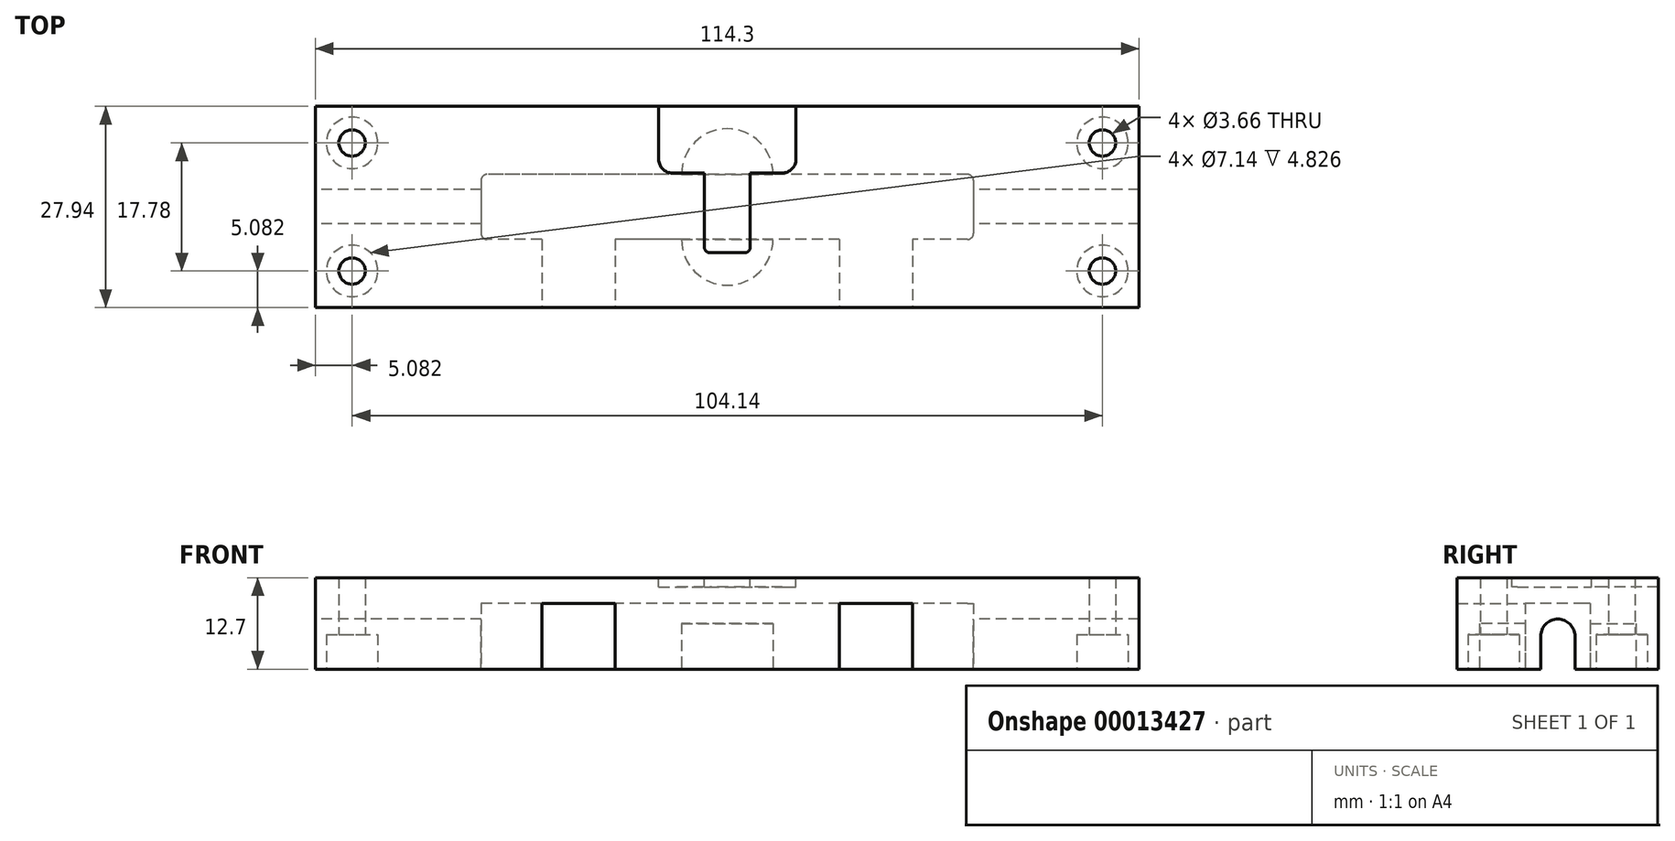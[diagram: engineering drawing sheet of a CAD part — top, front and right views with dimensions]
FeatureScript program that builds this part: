
annotation { "Feature Type Name" : "Feature", "Feature Type Description" : "" }
export const myFeature = defineFeature(function(context is Context, id is Id, definition is map)
    precondition{}
    {
        {
            var Q0;
            Q0=qCreatedBy(makeId("Top.planeOp"),FACE);
            var sketch = newSketch(context, id + "F0", { "sketchPlane" : qUnion([Q0])});
            skLineSegment(sketch, "E0.bottom", {"start": v(-44.98, -11.5) * mm, "end": v(69.32, -11.5) * mm});
            skLineSegment(sketch, "E0.top", {"start": v(-44.98, 16.43) * mm, "end": v(69.32, 16.43) * mm});
            skLineSegment(sketch, "E0.left", {"start": v(-44.98, -11.5) * mm, "end": v(-44.98, 16.43) * mm});
            skLineSegment(sketch, "E0.right", {"start": v(69.32, -11.5) * mm, "end": v(69.32, 16.43) * mm});
            skSolve(sketch);
        }
        {
            var Q0;
            Q0=makeQuery(id+"F0.imprint","IMPRINT",FACE,{"disambiguationData":[TD([[makeQuery(id+"F0.imprint","IMPRINT",EDGE,{"derivedFrom":sQuery(id+"F0.wireOp",EDGE,"E0.bottom")}),1.0]])]});
            extrude(context, id + "F1", {"entities" : qUnion([Q0]), "depth" : 12.7 * mm});
        }
        {
            var Q0;
            Q0=makeQuery(id+"F1.opExtrude","CAP_FACE",FACE,{"disambiguationData":[OSD([sQuery(id+"F0.wireOp",EDGE,"E0.bottom"),sQuery(id+"F0.wireOp",EDGE,"E0.top"),sQuery(id+"F0.wireOp",EDGE,"E0.left"),sQuery(id+"F0.wireOp",EDGE,"E0.right")])],"isStart":true});
            var sketch = newSketch(context, id + "F2", { "sketchPlane" : qUnion([Q0])});
            skLineSegment(sketch, "E1.bottom", {"start": v(45.52, -6.97) * mm, "end": v(-21.18, -6.97) * mm});
            skLineSegment(sketch, "E1.top", {"start": v(45.52, 2.05) * mm, "end": v(-21.18, 2.05) * mm});
            skLineSegment(sketch, "E1.left", {"start": v(46.33, -6.16) * mm, "end": v(46.33, 1.23) * mm});
            skLineSegment(sketch, "E1.right", {"start": v(-22, -6.16) * mm, "end": v(-22, 1.23) * mm});
            skPoint(sketch, "E2.visualSharp", {"position": v(46.33, -6.97) * mm});
            skArc(sketch, "E2.filletArc", {"start": v(45.52, -6.97) * mm, "mid": v(46.1, -6.73) * mm, "end": v(46.33, -6.16) * mm});
            skPoint(sketch, "E3.visualSharp", {"position": v(46.33, 2.05) * mm});
            skArc(sketch, "E3.filletArc", {"start": v(46.33, 1.23) * mm, "mid": v(46.1, 1.8) * mm, "end": v(45.52, 2.05) * mm});
            skPoint(sketch, "E4.visualSharp", {"position": v(-22, -6.97) * mm});
            skArc(sketch, "E4.filletArc", {"start": v(-22, -6.16) * mm, "mid": v(-21.75, -6.73) * mm, "end": v(-21.18, -6.97) * mm});
            skPoint(sketch, "E5.visualSharp", {"position": v(-22, 2.05) * mm});
            skArc(sketch, "E5.filletArc", {"start": v(-21.18, 2.05) * mm, "mid": v(-21.75, 1.8) * mm, "end": v(-22, 1.23) * mm});
            skSolve(sketch);
        }
        {
            var Q0;
            Q0=qSketchRegion(id+"F2",true);
            extrude(context, id + "F3", {"entities" : qUnion([Q0]), "operationType" : NewBodyOperationType.REMOVE, "oppositeDirection" : true, "depth" : 9.14 * mm});
        }
        {
            var Q0;
            Q0=makeQuery(id+"F1.opExtrude","SWEPT_FACE",FACE,{"disambiguationData":[OSD([sQuery(id+"F0.wireOp",EDGE,"E0.left")])]});
            var sketch = newSketch(context, id + "F4", { "sketchPlane" : qUnion([Q0])});
            skArc(sketch, "E6", {"start": v(-0.1, 4.57) * mm, "mid": v(-2.49, 6.95) * mm, "end": v(-4.87, 4.57) * mm});
            skLineSegment(sketch, "E7", {"start": v(-4.87, 4.57) * mm, "end": v(-4.87, 0) * mm});
            skLineSegment(sketch, "E8", {"start": v(-4.87, 0) * mm, "end": v(-0.1, 0) * mm});
            skLineSegment(sketch, "E9", {"start": v(-0.1, 0) * mm, "end": v(-0.1, 4.57) * mm});
            skSolve(sketch);
        }
        {
            var Q0;
            Q0=qSketchRegion(id+"F4",true);
            extrude(context, id + "F5", {"entities" : qUnion([Q0]), "operationType" : NewBodyOperationType.REMOVE, "endBound" : BoundingType.THROUGH_ALL, "oppositeDirection" : true, "depth" : 25.4 * mm});
        }
        {
            var Q0;
            {var subQ0=sQuery(id+"F0.wireOp",EDGE,"E0.bottom");var subQ1=sQuery(id+"F0.wireOp",EDGE,"E0.left");var subQ2=sQuery(id+"F0.wireOp",EDGE,"E0.right");Q0=makeQuery(id+"F5.boolean.opBoolean","SPLIT",FACE,{"disambiguationData":[TD([makeQuery(id+"F1.opExtrude","SWEPT_FACE",FACE,{"disambiguationData":[OSD([subQ0])]})])],"derivedFrom":makeQuery(id+"F1.opExtrude","CAP_FACE",FACE,{"disambiguationData":[OSD([subQ0,sQuery(id+"F0.wireOp",EDGE,"E0.top"),subQ1,subQ2])],"isStart":true})});}
            var sketch = newSketch(context, id + "F6", { "sketchPlane" : qUnion([Q0])});
            skArc(sketch, "E10", {"start": v(18.52, 2.05) * mm, "mid": v(12.17, 8.4) * mm, "end": v(5.82, 2.05) * mm});
            skArc(sketch, "E11", {"start": v(5.82, -6.97) * mm, "mid": v(12.17, -13.32) * mm, "end": v(18.52, -6.97) * mm});
            skLineSegment(sketch, "E12", {"start": v(5.82, 2.05) * mm, "end": v(5.82, -6.97) * mm});
            skLineSegment(sketch, "E13", {"start": v(18.52, 2.05) * mm, "end": v(18.52, -6.97) * mm});
            skSolve(sketch);
        }
        {
            var Q0;
            Q0=qSketchRegion(id+"F6",true);
            extrude(context, id + "F7", {"entities" : qUnion([Q0]), "operationType" : NewBodyOperationType.REMOVE, "oppositeDirection" : true, "depth" : 6.35 * mm});
        }
        {
            var Q0;
            {var subQ0=sQuery(id+"F0.wireOp",EDGE,"E0.bottom");var subQ1=sQuery(id+"F0.wireOp",EDGE,"E0.left");var subQ2=sQuery(id+"F0.wireOp",EDGE,"E0.right");Q0=makeQuery(id+"F5.boolean.opBoolean","SPLIT",FACE,{"disambiguationData":[TD([makeQuery(id+"F1.opExtrude","SWEPT_FACE",FACE,{"disambiguationData":[OSD([subQ0])]})])],"derivedFrom":makeQuery(id+"F1.opExtrude","CAP_FACE",FACE,{"disambiguationData":[OSD([subQ0,sQuery(id+"F0.wireOp",EDGE,"E0.top"),subQ1,subQ2])],"isStart":true})});}
            var sketch = newSketch(context, id + "F8", { "sketchPlane" : qUnion([Q0])});
            skLineSegment(sketch, "E14.top", {"start": v(37.9, 11.5) * mm, "end": v(27.74, 11.5) * mm});
            skLineSegment(sketch, "E14.left", {"start": v(37.9, 2.05) * mm, "end": v(37.9, 11.5) * mm});
            skLineSegment(sketch, "E14.right", {"start": v(27.74, 2.05) * mm, "end": v(27.74, 11.5) * mm});
            skLineSegment(sketch, "E15", {"start": v(37.9, 2.05) * mm, "end": v(27.74, 2.05) * mm});
            skSolve(sketch);
        }
        {
            var Q0;
            Q0=qSketchRegion(id+"F8",true);
            var Q1;
            Q1=makeQuery(id+"F3.boolean.opBoolean","COPY",FACE,{"derivedFrom":makeQuery(id+"F3.opExtrude","CAP_FACE",FACE,{"disambiguationData":[OSD([sQuery(id+"F2.wireOp",EDGE,"E1.bottom"),sQuery(id+"F2.wireOp",EDGE,"E1.top"),sQuery(id+"F2.wireOp",EDGE,"E1.left"),sQuery(id+"F2.wireOp",EDGE,"E1.right"),sQuery(id+"F2.wireOp",EDGE,"E2.filletArc"),sQuery(id+"F2.wireOp",EDGE,"E3.filletArc"),sQuery(id+"F2.wireOp",EDGE,"E4.filletArc"),sQuery(id+"F2.wireOp",EDGE,"E5.filletArc")])],"isStart":false})});
            extrude(context, id + "F9", {"entities" : qUnion([Q0]), "operationType" : NewBodyOperationType.REMOVE, "endBound" : BoundingType.UP_TO_SURFACE, "oppositeDirection" : true, "endBoundEntityFace" : qUnion([Q1]), "depth" : 25.4 * mm});
        }
        {
            var Q0;
            {var subQ0=sQuery(id+"F0.wireOp",EDGE,"E0.bottom");var subQ1=sQuery(id+"F0.wireOp",EDGE,"E0.left");var subQ2=sQuery(id+"F0.wireOp",EDGE,"E0.right");var subQ7=makeQuery(id+"F1.opExtrude","SWEPT_FACE",FACE,{"disambiguationData":[OSD([subQ1])]});var subQ8=makeQuery(id+"F1.opExtrude","SWEPT_FACE",FACE,{"disambiguationData":[OSD([subQ0])]});Q0=makeQuery(id+"F9.boolean.opBoolean","SPLIT",FACE,{"disambiguationData":[TD([subQ7])],"derivedFrom":makeQuery(id+"F5.boolean.opBoolean","SPLIT",FACE,{"disambiguationData":[TD([subQ8])],"derivedFrom":makeQuery(id+"F1.opExtrude","CAP_FACE",FACE,{"disambiguationData":[OSD([subQ0,sQuery(id+"F0.wireOp",EDGE,"E0.top"),subQ1,subQ2])],"isStart":true})})});}
            var sketch = newSketch(context, id + "F10", { "sketchPlane" : qUnion([Q0])});
            skLineSegment(sketch, "E16.bottom", {"start": v(-3.4, 2.05) * mm, "end": v(-13.56, 2.05) * mm});
            skLineSegment(sketch, "E16.top", {"start": v(-3.4, 11.5) * mm, "end": v(-13.56, 11.5) * mm});
            skLineSegment(sketch, "E16.left", {"start": v(-3.4, 2.05) * mm, "end": v(-3.4, 11.5) * mm});
            skLineSegment(sketch, "E16.right", {"start": v(-13.56, 2.05) * mm, "end": v(-13.56, 11.5) * mm});
            skSolve(sketch);
        }
        {
            var Q0;
            Q0=qSketchRegion(id+"F10",true);
            var Q1;
            Q1=makeQuery(id+"F9.boolean.opBoolean","MERGE",FACE,{"derivedFrom":[makeQuery(id+"F3.boolean.opBoolean","COPY",FACE,{"derivedFrom":makeQuery(id+"F3.opExtrude","CAP_FACE",FACE,{"disambiguationData":[OSD([sQuery(id+"F2.wireOp",EDGE,"E1.bottom"),sQuery(id+"F2.wireOp",EDGE,"E1.top"),sQuery(id+"F2.wireOp",EDGE,"E1.left"),sQuery(id+"F2.wireOp",EDGE,"E1.right"),sQuery(id+"F2.wireOp",EDGE,"E2.filletArc"),sQuery(id+"F2.wireOp",EDGE,"E3.filletArc"),sQuery(id+"F2.wireOp",EDGE,"E4.filletArc"),sQuery(id+"F2.wireOp",EDGE,"E5.filletArc")])],"isStart":false})}),makeQuery(id+"F9.opExtrude","CAP_FACE",FACE,{"disambiguationData":[OSD([sQuery(id+"F8.wireOp",EDGE,"E14.top"),sQuery(id+"F8.wireOp",EDGE,"E14.left"),sQuery(id+"F8.wireOp",EDGE,"E14.right"),sQuery(id+"F8.wireOp",EDGE,"E15")])],"isStart":false})]});
            extrude(context, id + "F11", {"entities" : qUnion([Q0]), "operationType" : NewBodyOperationType.REMOVE, "endBound" : BoundingType.UP_TO_SURFACE, "oppositeDirection" : true, "endBoundEntityFace" : qUnion([Q1]), "depth" : 6.6 * mm});
        }
        {
            var Q0;
            {var subQ0=sQuery(id+"F0.wireOp",EDGE,"E0.top");var subQ1=sQuery(id+"F0.wireOp",EDGE,"E0.left");var subQ2=sQuery(id+"F0.wireOp",EDGE,"E0.right");Q0=makeQuery(id+"F5.boolean.opBoolean","SPLIT",FACE,{"disambiguationData":[TD([makeQuery(id+"F1.opExtrude","SWEPT_FACE",FACE,{"disambiguationData":[OSD([subQ0])]})])],"derivedFrom":makeQuery(id+"F1.opExtrude","CAP_FACE",FACE,{"disambiguationData":[OSD([sQuery(id+"F0.wireOp",EDGE,"E0.bottom"),subQ0,subQ1,subQ2])],"isStart":true})});}
            var sketch = newSketch(context, id + "F12", { "sketchPlane" : qUnion([Q0])});
            skPoint(sketch, "E17", {"position": v(64.24, -11.35) * mm});
            skPoint(sketch, "E18", {"position": v(64.24, 6.43) * mm});
            skPoint(sketch, "E19", {"position": v(-39.9, -11.35) * mm});
            skPoint(sketch, "E20", {"position": v(-39.9, 6.43) * mm});
            skSolve(sketch);
        }
        {
            var Q0;
            Q0=sQuery(id+"F12.wireOp",VERTEX,"E17");
            var Q1;
            Q1=sQuery(id+"F12.wireOp",VERTEX,"E18");
            var Q2;
            Q2=sQuery(id+"F12.wireOp",VERTEX,"E19");
            var Q3;
            Q3=sQuery(id+"F12.wireOp",VERTEX,"E20");
            var Q4;
            Q4=makeQuery(id+"FvrC87ADXBSDjqa_1.boolean.opBoolean","SPLIT",BODY,{"disambiguationData":[OD(0.0)],"derivedFrom":makeQuery(id+"F1.opExtrude","SWEPT_BODY",BODY,{"disambiguationData":[OSD([sQuery(id+"F0.wireOp",EDGE,"E0.bottom"),sQuery(id+"F0.wireOp",EDGE,"E0.top"),sQuery(id+"F0.wireOp",EDGE,"E0.left"),sQuery(id+"F0.wireOp",EDGE,"E0.right")])]})});
            hole(context, id + "F13", {"style" : HoleStyle.C_BORE, "holeDiameter" : 3.66 * mm, "cBoreDiameter" : 7.14 * mm, "cBoreDepth" : 4.83 * mm, "endStyle" : HoleEndStyle.THROUGH, "locations" : qUnion([Q0, Q1, Q2, Q3]), "scope" : qUnion([Q4])});
        }
        {
            var Q0;
            Q0=makeQuery(id+"F1.opExtrude","CAP_FACE",FACE,{"disambiguationData":[OSD([sQuery(id+"F0.wireOp",EDGE,"E0.bottom"),sQuery(id+"F0.wireOp",EDGE,"E0.top"),sQuery(id+"F0.wireOp",EDGE,"E0.left"),sQuery(id+"F0.wireOp",EDGE,"E0.right")])],"isStart":false});
            var sketch = newSketch(context, id + "F14", { "sketchPlane" : qUnion([Q0])});
            skLineSegment(sketch, "E21", {"start": v(15.35, 7.18) * mm, "end": v(15.35, 7.18) * mm});
            skPoint(sketch, "E22.visualSharp", {"position": v(15.35, 7.18) * mm});
            skPoint(sketch, "E23.visualSharp", {"position": v(9, -3.89) * mm});
            skPoint(sketch, "E24.visualSharp", {"position": v(9, 7.18) * mm});
            skLineSegment(sketch, "E25.left", {"start": v(15.35, -3.13) * mm, "end": v(15.35, 7.18) * mm});
            skLineSegment(sketch, "E25.right", {"start": v(9, -3.13) * mm, "end": v(9, 7.18) * mm});
            skLineSegment(sketch, "E26", {"start": v(2.65, 9.08) * mm, "end": v(2.65, 16.43) * mm});
            skLineSegment(sketch, "E27", {"start": v(2.65, 16.43) * mm, "end": v(21.7, 16.43) * mm});
            skLineSegment(sketch, "E28", {"start": v(21.7, 16.43) * mm, "end": v(21.7, 9.08) * mm});
            skLineSegment(sketch, "E29", {"start": v(19.8, 7.18) * mm, "end": v(15.35, 7.18) * mm});
            skArc(sketch, "E30.filletArc", {"start": v(19.8, 7.18) * mm, "mid": v(21.14, 7.74) * mm, "end": v(21.7, 9.08) * mm});
            skPoint(sketch, "E31.visualSharp", {"position": v(15.35, -3.89) * mm});
            skLineSegment(sketch, "E32.trimOffspring", {"start": v(9, 7.18) * mm, "end": v(4.55, 7.18) * mm});
            skLineSegment(sketch, "E33", {"start": v(9, 7.18) * mm, "end": v(9, 7.18) * mm});
            skPoint(sketch, "E30.visualSharp", {"position": v(21.7, 7.18) * mm});
            skPoint(sketch, "E34.visualSharp", {"position": v(2.65, 7.18) * mm});
            skArc(sketch, "E34.filletArc", {"start": v(2.65, 9.08) * mm, "mid": v(3.2, 7.74) * mm, "end": v(4.55, 7.18) * mm});
            skLineSegment(sketch, "E25.bottom", {"start": v(14.58, -3.89) * mm, "end": v(9.76, -3.89) * mm});
            skArc(sketch, "E31.filletArc", {"start": v(14.58, -3.89) * mm, "mid": v(15.12, -3.66) * mm, "end": v(15.35, -3.13) * mm});
            skArc(sketch, "E23.filletArc", {"start": v(9, -3.13) * mm, "mid": v(9.22, -3.66) * mm, "end": v(9.76, -3.89) * mm});
            skSolve(sketch);
        }
        {
            var Q0;
            Q0 = qSketchRegion(id + "F14", true);
            var Q1;
            Q1=makeQuery(id+"FXOkJv0ckkrfQTb_1.boolean.opBoolean","COPY",FACE,{"derivedFrom":makeQuery(id+"FXOkJv0ckkrfQTb_1.opExtrude","CAP_FACE",FACE,{"disambiguationData":[OSD([sQuery(id+"FNH8KqWSbUaVyww_1.wireOp",EDGE,"95eef0d6-668e-4bf6-a172-0342ca8e1830.bottom"),sQuery(id+"FNH8KqWSbUaVyww_1.wireOp",EDGE,"95eef0d6-668e-4bf6-a172-0342ca8e1830.top"),sQuery(id+"FNH8KqWSbUaVyww_1.wireOp",EDGE,"95eef0d6-668e-4bf6-a172-0342ca8e1830.left"),sQuery(id+"FNH8KqWSbUaVyww_1.wireOp",EDGE,"95eef0d6-668e-4bf6-a172-0342ca8e1830.right"),sQuery(id+"FNH8KqWSbUaVyww_1.wireOp",EDGE,"d7b8f0e6-89bf-4d90-9a0f-a7446f85b501.bottom"),sQuery(id+"FNH8KqWSbUaVyww_1.wireOp",EDGE,"d7b8f0e6-89bf-4d90-9a0f-a7446f85b501.top"),sQuery(id+"FNH8KqWSbUaVyww_1.wireOp",EDGE,"d7b8f0e6-89bf-4d90-9a0f-a7446f85b501.left"),sQuery(id+"FNH8KqWSbUaVyww_1.wireOp",EDGE,"d7b8f0e6-89bf-4d90-9a0f-a7446f85b501.right"),sQuery(id+"FNH8KqWSbUaVyww_1.wireOp",EDGE,"efd13bb3-fbc7-4de9-8f96-348dde713d37.filletArc"),sQuery(id+"FNH8KqWSbUaVyww_1.wireOp",EDGE,"7ac8e13b-5649-4a3d-91c6-297c25820bfb.filletArc"),sQuery(id+"FNH8KqWSbUaVyww_1.wireOp",EDGE,"2ec1616d-3554-4afe-808e-9cb3dce9970b.filletArc"),sQuery(id+"FNH8KqWSbUaVyww_1.wireOp",EDGE,"5c109569-0ffe-45b0-9409-798be332c4d6.filletArc")])],"isStart":false})});
            extrude(context, id + "F15", {"entities" : qUnion([Q0]), "operationType" : NewBodyOperationType.REMOVE, "oppositeDirection" : true, "endBoundEntity" : qUnion([Q1]), "depth" : 1.27 * mm});
        }
    });
